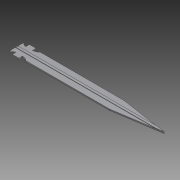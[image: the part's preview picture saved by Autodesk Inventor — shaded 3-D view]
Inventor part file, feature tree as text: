
AUTODESK INVENTOR PART (.ipt)
format: ipt  version: 2011 (Build 150239000, 239)  size: 285,184 bytes
history: native  units: mm
features: fillet x4, other x2, extrude x2, sketch x2
ambient origin geometry x8: Origin, YZ Plane, XZ Plane, XY Plane, X Axis, Y Axis, Z Axis, Center Point
feature tree (10):
  other  "Sólido1"
  extrude  "Extrusión1"  Depth=12.0mm
  extrude  "Extrusión2"  Depth=3.2mm
  fillet  "Empalme1"  Radius=9.5mm
  fillet  "Empalme2"  Radius=6.5mm
  fillet  "Empalme3"  Radius=8.0mm
  fillet  "Empalme4"  Radius=5.0mm
  other  "Mitad"
  sketch  "Boceto1"  dims[d0=21.6mm d2=12.0mm]
  sketch  "Boceto2"  dims[d3=1.0mm d8=3.2mm d15=9.5mm d17=6.5mm d18=8.0mm d19=5.0mm d20=3.2mm d21=12.0mm d23=70.0mm d24=2.0mm d25=0.0mm d26=3.4mm d27=0.7mm d28=0.0mm d29=2.5mm d30=1.0mm d31=0.5mm d32=3.0mm d35=3.061574mm d36=1.530787mm d43=150.0mm d44=220.0mm]
